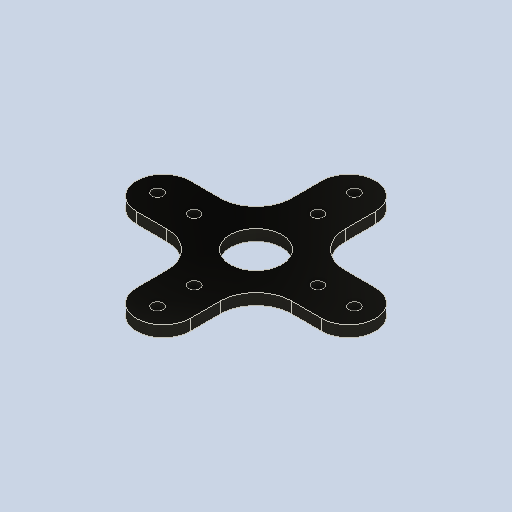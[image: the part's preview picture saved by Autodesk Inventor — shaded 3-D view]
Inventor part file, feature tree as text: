
AUTODESK INVENTOR PART (.ipt)
format: ipt  version: 2025.1 (Build 291241020, 241B)  size: 172,032 bytes
history: native  units: in
note: dims shown in document units (in); Inventor stores cm internally (conversion verified against a paired STEP export)
features: sketch x2, extrude x1, other x1
ambient origin geometry x8: Origin, YZ Plane, XZ Plane, XY Plane, X Axis, Y Axis, Z Axis, Center Point
bodies: Solid1 (feature_tree)
feature tree (4):
  extrude  "Extrusion1"  Depth=0.1575in
  sketch  "Sketch1"  dims[d0=1.5748in d2=360.0deg d4=0.1575in]
  sketch  "Sketch Circular Pattern1"  dims[d5=0.8661in d6=1.378in d7=0.7232in d39=0.375in d41=0.375in d46=0.5in d50=0.1575in d51=0.0in]
  other  "Image1"
